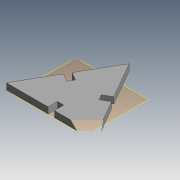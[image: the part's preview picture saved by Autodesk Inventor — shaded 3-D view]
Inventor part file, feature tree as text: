
AUTODESK INVENTOR PART (.ipt)
format: ipt  version: 2014 SP1 (Build 180222100, 222)  size: 89,088 bytes
history: native  units: in
note: dims shown in document units (in); Inventor stores cm internally (conversion verified against a paired STEP export)
features: plane x1, extrude x1, sketch x1
ambient origin geometry x8: Origin, YZ Plane, XZ Plane, XY Plane, X Axis, Y Axis, Z Axis, Center Point
bodies: Body1 (feature_tree)
feature tree (3):
  plane  "Work Plane1"
  extrude  "Extrusion2"  Depth=0.2228in
  sketch  "Sketch1"  dims[d5=60.0deg d6=120.0deg d34=1.5748in d35=0.4075in d36=1.1811in d38=360.0deg d40=0.2228in d41=0.0in]
